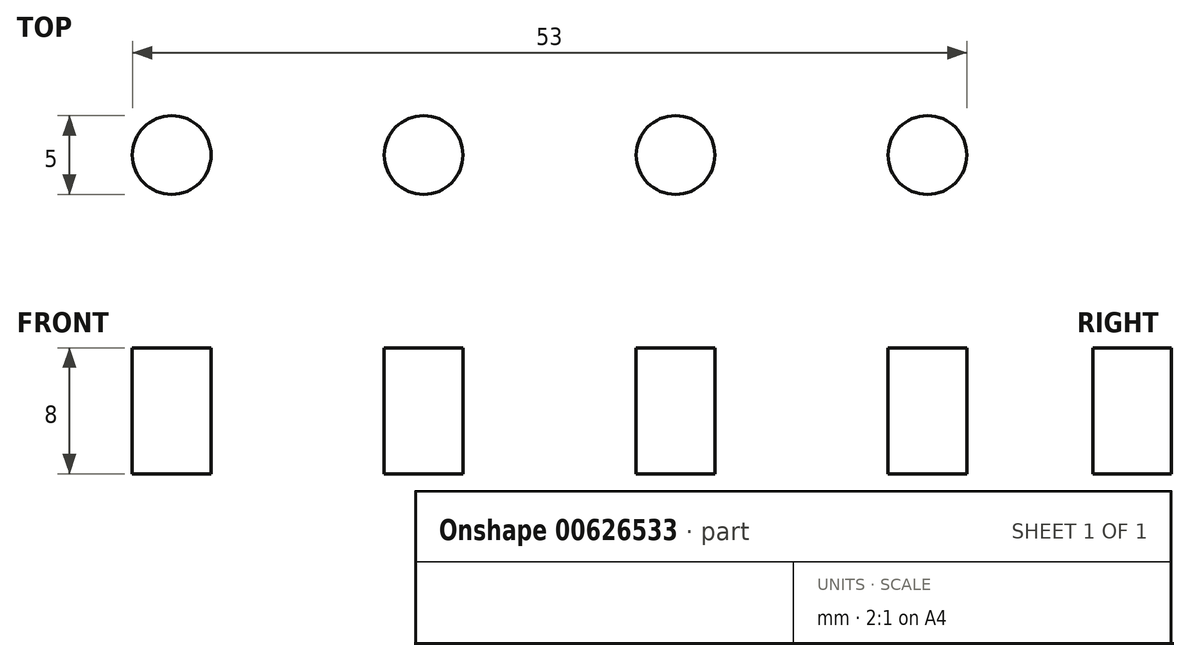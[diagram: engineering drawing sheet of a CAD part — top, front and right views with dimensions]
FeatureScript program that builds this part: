
annotation { "Feature Type Name" : "Feature", "Feature Type Description" : "" }
export const myFeature = defineFeature(function(context is Context, id is Id, definition is map)
    precondition{}
    {
        {
            var Q0;
            Q0=qCreatedBy(makeId("Top.planeOp"),FACE);
            var sketch = newSketch(context, id + "F0", { "sketchPlane" : qUnion([Q0])});
            skCircle(sketch, "E0", {"center": v(-13.9, -20.18) * mm, "radius": 2.5 * mm});
            skSolve(sketch);
        }
        {
            var Q0;
            Q0 = qSketchRegion(id + "F0", true);
            extrude(context, id + "F1", {"entities" : qUnion([Q0]), "depth" : 8 * mm, "offsetDistance" : 25 * mm});
        }
        {
            var Q0;
            Q0=makeQuery(id+"F1.opExtrude","SWEPT_BODY",BODY,{"disambiguationData":[OSD([sQuery(id+"F0.wireOp",EDGE,"E0")])]});
            transform(context, id + "F2", {"entities" : qUnion([Q0]), "transformType" : TransformType.TRANSLATION_3D, "dx" : 16 * mm, "dy" : 0 * mm, "dz" : 0 * mm, "makeCopy" : true});
        }
        {
            var Q0;
            Q0=makeQuery(id+"F2.opPattern","COPY",BODY,{"derivedFrom":makeQuery(id+"F1.opExtrude","SWEPT_BODY",BODY,{"disambiguationData":[OSD([sQuery(id+"F0.wireOp",EDGE,"E0")])]}),"instanceName":"1"});
            transform(context, id + "F3", {"entities" : qUnion([Q0]), "transformType" : TransformType.TRANSLATION_3D, "dx" : 16 * mm, "dy" : 0 * mm, "dz" : 0 * mm, "makeCopy" : true});
        }
        {
            var Q0;
            Q0=makeQuery(id+"F3.opPattern","COPY",BODY,{"derivedFrom":makeQuery(id+"F2.opPattern","COPY",BODY,{"derivedFrom":makeQuery(id+"F1.opExtrude","SWEPT_BODY",BODY,{"disambiguationData":[OSD([sQuery(id+"F0.wireOp",EDGE,"E0")])]}),"instanceName":"1"}),"instanceName":"1"});
            transform(context, id + "F4", {"entities" : qUnion([Q0]), "transformType" : TransformType.TRANSLATION_3D, "dx" : 16 * mm, "dy" : 0 * mm, "dz" : 0 * mm, "makeCopy" : true});
        }
    });
